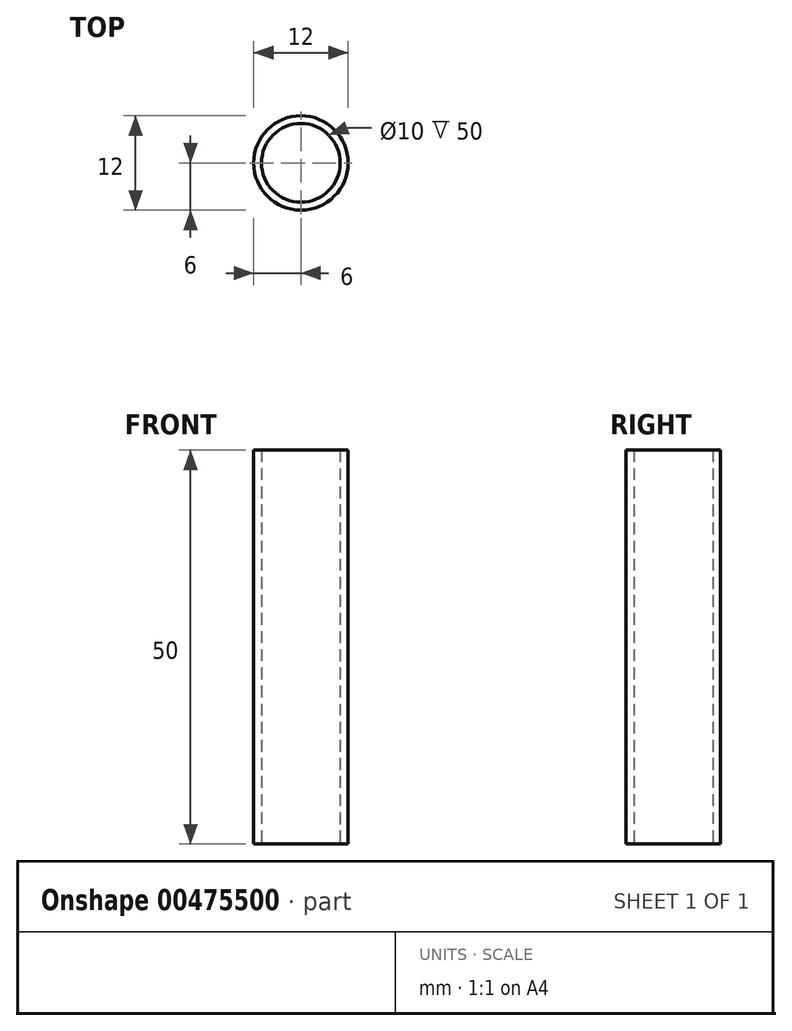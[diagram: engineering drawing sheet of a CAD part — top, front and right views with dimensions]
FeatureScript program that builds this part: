
annotation { "Feature Type Name" : "Feature", "Feature Type Description" : "" }
export const myFeature = defineFeature(function(context is Context, id is Id, definition is map)
    precondition{}
    {
        {
            var Q0;
            Q0=qCreatedBy(makeId("Top.planeOp"),FACE);
            var sketch = newSketch(context, id + "F0", { "sketchPlane" : qUnion([Q0])});
            skCircle(sketch, "E0", {"center": v(0, 0) * mm, "radius": 5 * mm});
            skCircle(sketch, "E1", {"center": v(0, 0) * mm, "radius": 6 * mm});
            skSolve(sketch);
        }
        {
            var Q0;
            Q0=makeQuery(id+"F0.imprint","IMPRINT",FACE,{"disambiguationData":[TD([[makeQuery(id+"F0.imprint","IMPRINT",EDGE,{"derivedFrom":sQuery(id+"F0.wireOp",EDGE,"E0")}),-1.0]])]});
            extrude(context, id + "F1", {"entities" : qUnion([Q0]), "depth" : 50 * mm, "offsetDistance" : 25 * mm});
        }
    });
